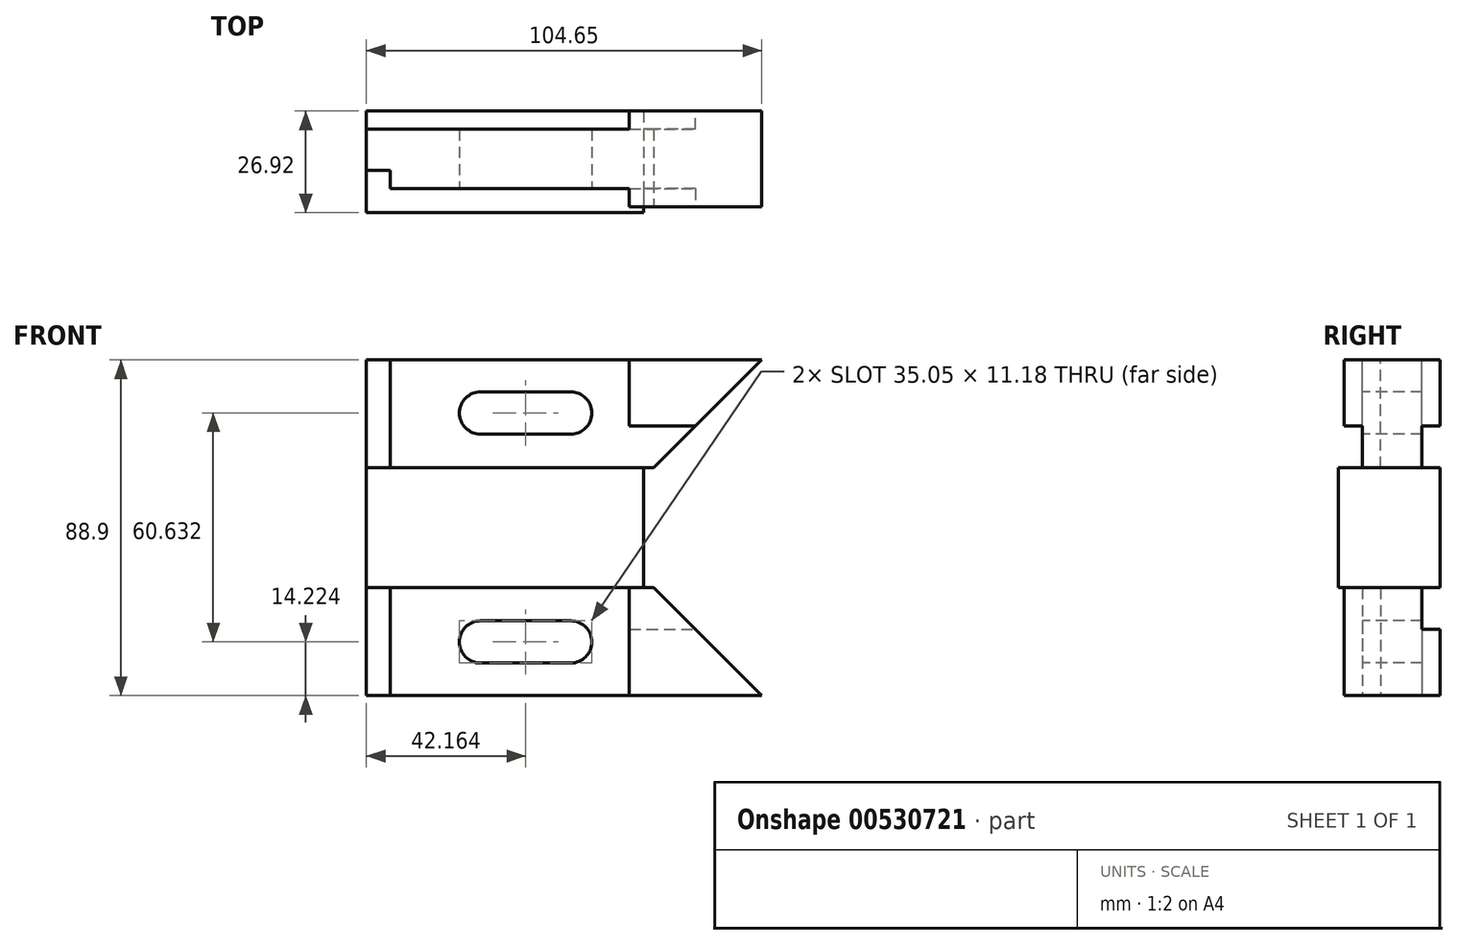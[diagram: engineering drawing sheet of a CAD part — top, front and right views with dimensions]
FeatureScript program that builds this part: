
annotation { "Feature Type Name" : "Feature", "Feature Type Description" : "" }
export const myFeature = defineFeature(function(context is Context, id is Id, definition is map)
    precondition{}
    {
        {
            var Q0;
            Q0=qCreatedBy(makeId("Right.planeOp"),FACE);
            var sketch = newSketch(context, id + "F0", { "sketchPlane" : qUnion([Q0])});
            skLineSegment(sketch, "E0", {"start": v(0, 0) * mm, "end": v(25.4, 0) * mm});
            skLineSegment(sketch, "E1", {"start": v(25.4, 0) * mm, "end": v(25.4, 28.58) * mm});
            skLineSegment(sketch, "E2", {"start": v(0, 0) * mm, "end": v(0, 28.58) * mm});
            skLineSegment(sketch, "E3", {"start": v(25.4, 60.33) * mm, "end": v(25.4, 88.9) * mm});
            skLineSegment(sketch, "E4", {"start": v(0, 60.33) * mm, "end": v(0, 88.9) * mm});
            skLineSegment(sketch, "E5", {"start": v(0, 88.9) * mm, "end": v(25.4, 88.9) * mm});
            skLineSegment(sketch, "E6", {"start": v(0, 28.58) * mm, "end": v(-1.52, 28.58) * mm});
            skLineSegment(sketch, "E7", {"start": v(-1.52, 28.58) * mm, "end": v(-1.52, 60.33) * mm});
            skLineSegment(sketch, "E8", {"start": v(0, 60.33) * mm, "end": v(-1.52, 60.33) * mm});
            skLineSegment(sketch, "E9", {"start": v(25.4, 60.33) * mm, "end": v(26.92, 60.33) * mm});
            skLineSegment(sketch, "E10", {"start": v(25.4, 28.58) * mm, "end": v(26.92, 28.58) * mm});
            skLineSegment(sketch, "E11", {"start": v(26.92, 60.33) * mm, "end": v(26.92, 28.58) * mm});
            skSolve(sketch);
        }
        {
            var Q0;
            Q0=qSketchRegion(id+"F0",true);
            extrude(context, id + "F1", {"entities" : qUnion([Q0]), "depth" : 104.65 * mm});
        }
        {
            var Q0;
            Q0=makeQuery(id+"F1.opExtrude","SWEPT_FACE",FACE,{"disambiguationData":[OSD([sQuery(id+"F0.wireOp",EDGE,"E5")])]});
            var sketch = newSketch(context, id + "F2", { "sketchPlane" : qUnion([Q0])});
            skLineSegment(sketch, "E12.0.0", {"start": v(0, 0) * mm, "end": v(0, -1.52) * mm});
            skLineSegment(sketch, "E12.0.1", {"start": v(0, -1.52) * mm, "end": v(104.65, -1.52) * mm});
            skLineSegment(sketch, "E12.0.2", {"start": v(104.65, -1.52) * mm, "end": v(104.65, 0) * mm});
            skLineSegment(sketch, "E12.0.3", {"start": v(104.65, 0) * mm, "end": v(0, 0) * mm});
            skLineSegment(sketch, "E13", {"start": v(0, -1.52) * mm, "end": v(0, 4.83) * mm});
            skLineSegment(sketch, "E14.0.0", {"start": v(0, 26.92) * mm, "end": v(0, 25.4) * mm});
            skLineSegment(sketch, "E14.0.1", {"start": v(0, 25.4) * mm, "end": v(104.65, 25.4) * mm});
            skLineSegment(sketch, "E14.0.2", {"start": v(104.65, 25.4) * mm, "end": v(104.65, 26.92) * mm});
            skLineSegment(sketch, "E14.0.3", {"start": v(104.65, 26.92) * mm, "end": v(0, 26.92) * mm});
            skLineSegment(sketch, "E15", {"start": v(0, 26.92) * mm, "end": v(0, 20.57) * mm});
            skLineSegment(sketch, "E16", {"start": v(0, 4.83) * mm, "end": v(0, 9.65) * mm});
            skLineSegment(sketch, "E17", {"start": v(0, 9.65) * mm, "end": v(6.35, 9.65) * mm});
            skLineSegment(sketch, "E18", {"start": v(6.35, 9.65) * mm, "end": v(6.35, 4.83) * mm});
            skLineSegment(sketch, "E19", {"start": v(6.35, 4.83) * mm, "end": v(69.6, 4.83) * mm});
            skLineSegment(sketch, "E20", {"start": v(0, 20.57) * mm, "end": v(69.6, 20.57) * mm});
            skLineSegment(sketch, "E21", {"start": v(69.6, 20.57) * mm, "end": v(69.6, 25.4) * mm});
            skLineSegment(sketch, "E22", {"start": v(69.6, 4.83) * mm, "end": v(69.6, 0) * mm});
            skLineSegment(sketch, "E23", {"start": v(0, -1.52) * mm, "end": v(73.4, -1.52) * mm});
            skLineSegment(sketch, "E24", {"start": v(73.4, -1.52) * mm, "end": v(73.4, 0) * mm});
            skLineSegment(sketch, "E25", {"start": v(73.4, 0) * mm, "end": v(0, 0) * mm});
            skLineSegment(sketch, "E26", {"start": v(0, 25.4) * mm, "end": v(0, 26.92) * mm});
            skLineSegment(sketch, "E27", {"start": v(0, 26.92) * mm, "end": v(73.4, 26.92) * mm});
            skLineSegment(sketch, "E28", {"start": v(73.4, 26.92) * mm, "end": v(73.4, 25.4) * mm});
            skLineSegment(sketch, "E29", {"start": v(73.4, 25.4) * mm, "end": v(0, 25.4) * mm});
            skSolve(sketch);
        }
        {
            var Q0;
            {var subQ0=sQuery(id+"F2.wireOp",EDGE,"E15");Q0=makeQuery(id+"F2.imprint","IMPRINT",FACE,{"disambiguationData":[TD([[makeQuery(id+"F2.imprint","IMPRINT",EDGE,{"derivedFrom":subQ0}),-1.0]])]});}
            var Q1;
            {var subQ0=sQuery(id+"F2.wireOp",EDGE,"E16");Q1=makeQuery(id+"F2.imprint","IMPRINT",FACE,{"disambiguationData":[TD([[makeQuery(id+"F2.imprint","IMPRINT",EDGE,{"derivedFrom":subQ0}),-1.0]])]});}
            extrude(context, id + "F3", {"entities" : qUnion([Q0, Q1]), "operationType" : NewBodyOperationType.REMOVE, "oppositeDirection" : true, "depth" : 28.57 * mm});
        }
        {
            var Q0;
            Q0=makeQuery(id+"F2.imprint","IMPRINT",FACE,{"disambiguationData":[TD([[makeQuery(id+"F2.imprint","IMPRINT",EDGE,{"derivedFrom":sQuery(id+"F2.wireOp",EDGE,"E14.0.1")}),-1.0]])]});
            var Q1;
            Q1=makeQuery(id+"F2.imprint","IMPRINT",FACE,{"disambiguationData":[TD([[makeQuery(id+"F2.imprint","IMPRINT",EDGE,{"derivedFrom":sQuery(id+"F2.wireOp",EDGE,"E12.0.1")}),1.0]])]});
            extrude(context, id + "F4", {"entities" : qUnion([Q0, Q1]), "operationType" : NewBodyOperationType.REMOVE, "oppositeDirection" : true, "depth" : 88.9 * mm});
        }
        {
            var Q0;
            Q0=makeQuery(id+"F1.opExtrude","SWEPT_FACE",FACE,{"disambiguationData":[OSD([sQuery(id+"F0.wireOp",EDGE,"E0")])]});
            var sketch = newSketch(context, id + "F5", { "sketchPlane" : qUnion([Q0])});
            skLineSegment(sketch, "E30.0", {"start": v(6.35, -4.83) * mm, "end": v(69.6, -4.83) * mm});
            skPoint(sketch, "E31.0", {"position": v(6.35, -9.65) * mm});
            skPoint(sketch, "E32.0", {"position": v(3.18, -9.65) * mm});
            skLineSegment(sketch, "E33.0", {"start": v(0, -9.65) * mm, "end": v(0, -20.57) * mm});
            skLineSegment(sketch, "E34.0", {"start": v(0, -20.57) * mm, "end": v(69.6, -20.57) * mm});
            skLineSegment(sketch, "E35.0", {"start": v(104.65, -25.4) * mm, "end": v(69.6, -25.4) * mm});
            skPoint(sketch, "E36.0", {"position": v(69.6, -22.99) * mm});
            skLineSegment(sketch, "E37.0", {"start": v(104.65, 0) * mm, "end": v(69.6, 0) * mm});
            skLineSegment(sketch, "E38.0", {"start": v(69.6, -4.83) * mm, "end": v(69.6, 0) * mm});
            skLineSegment(sketch, "E39.0", {"start": v(69.6, -20.57) * mm, "end": v(69.6, -25.4) * mm});
            skLineSegment(sketch, "E40.0.0", {"start": v(73.4, -25.4) * mm, "end": v(73.4, -26.92) * mm});
            skLineSegment(sketch, "E40.0.1", {"start": v(73.4, -26.92) * mm, "end": v(0, -26.92) * mm});
            skLineSegment(sketch, "E40.0.2", {"start": v(0, -26.92) * mm, "end": v(0, -20.57) * mm});
            skLineSegment(sketch, "E40.0.5", {"start": v(69.6, -25.4) * mm, "end": v(73.4, -25.4) * mm});
            skLineSegment(sketch, "E41.0.0", {"start": v(73.4, 1.52) * mm, "end": v(73.4, 0) * mm});
            skLineSegment(sketch, "E41.0.1", {"start": v(73.4, 0) * mm, "end": v(69.6, 0) * mm});
            skLineSegment(sketch, "E41.0.2", {"start": v(69.6, 0) * mm, "end": v(69.6, -4.83) * mm});
            skLineSegment(sketch, "E41.0.3", {"start": v(69.6, -4.83) * mm, "end": v(6.35, -4.83) * mm});
            skLineSegment(sketch, "E41.0.4", {"start": v(6.35, -4.83) * mm, "end": v(6.35, -9.65) * mm});
            skLineSegment(sketch, "E41.0.5", {"start": v(6.35, -9.65) * mm, "end": v(0, -9.65) * mm});
            skLineSegment(sketch, "E41.0.6", {"start": v(0, -9.65) * mm, "end": v(0, 1.52) * mm});
            skLineSegment(sketch, "E41.0.7", {"start": v(0, 1.52) * mm, "end": v(73.4, 1.52) * mm});
            skSolve(sketch);
        }
        {
            var Q0;
            Q0=qSketchRegion(id+"F5",true);
            extrude(context, id + "F6", {"entities" : qUnion([Q0]), "operationType" : NewBodyOperationType.REMOVE, "oppositeDirection" : true, "depth" : 28.57 * mm});
        }
        {
            var Q0;
            Q0=makeQuery(id+"F4.boolean.opBoolean","MERGE",FACE,{"derivedFrom":[makeQuery(id+"F1.opExtrude","SWEPT_FACE",FACE,{"disambiguationData":[OSD([sQuery(id+"F0.wireOp",EDGE,"E2")])]}),makeQuery(id+"F1.opExtrude","SWEPT_FACE",FACE,{"disambiguationData":[OSD([sQuery(id+"F0.wireOp",EDGE,"E4")])]}),makeQuery(id+"F4.opExtrude","SWEPT_FACE",FACE,{"disambiguationData":[OSD([sQuery(id+"F2.wireOp",EDGE,"E12.0.3")])]})]});
            var sketch = newSketch(context, id + "F7", { "sketchPlane" : qUnion([Q0])});
            skLineSegment(sketch, "E42.0", {"start": v(104.65, 88.9) * mm, "end": v(69.6, 88.9) * mm});
            skLineSegment(sketch, "E43.0", {"start": v(69.6, 71.37) * mm, "end": v(69.6, 88.9) * mm});
            skLineSegment(sketch, "E44.0", {"start": v(6.35, 88.9) * mm, "end": v(69.6, 88.9) * mm});
            skLineSegment(sketch, "E45.0.0", {"start": v(69.6, 88.9) * mm, "end": v(6.35, 88.9) * mm});
            skLineSegment(sketch, "E45.0.1", {"start": v(6.35, 88.9) * mm, "end": v(6.35, 60.33) * mm});
            skLineSegment(sketch, "E45.0.2", {"start": v(6.35, 60.33) * mm, "end": v(69.6, 60.33) * mm});
            skLineSegment(sketch, "E46.0.0", {"start": v(0, 28.58) * mm, "end": v(73.4, 28.58) * mm});
            skLineSegment(sketch, "E46.0.1", {"start": v(73.4, 28.58) * mm, "end": v(73.4, 60.33) * mm});
            skLineSegment(sketch, "E46.0.2", {"start": v(73.4, 60.33) * mm, "end": v(0, 60.33) * mm});
            skLineSegment(sketch, "E46.0.3", {"start": v(0, 60.33) * mm, "end": v(0, 28.58) * mm});
            skLineSegment(sketch, "E47.0.0", {"start": v(6.35, 0) * mm, "end": v(69.6, 0) * mm});
            skLineSegment(sketch, "E47.0.1", {"start": v(69.6, 0) * mm, "end": v(69.6, 28.58) * mm});
            skLineSegment(sketch, "E47.0.2", {"start": v(69.6, 28.58) * mm, "end": v(6.35, 28.58) * mm});
            skLineSegment(sketch, "E47.0.3", {"start": v(6.35, 28.58) * mm, "end": v(6.35, 0) * mm});
            skLineSegment(sketch, "E48.0.0", {"start": v(73.4, 60.33) * mm, "end": v(73.4, 28.58) * mm});
            skLineSegment(sketch, "E48.0.1", {"start": v(73.4, 28.58) * mm, "end": v(69.6, 28.58) * mm});
            skLineSegment(sketch, "E48.0.2", {"start": v(69.6, 28.58) * mm, "end": v(69.6, 0) * mm});
            skLineSegment(sketch, "E48.0.3", {"start": v(69.6, 0) * mm, "end": v(104.65, 0) * mm});
            skLineSegment(sketch, "E48.0.4", {"start": v(104.65, 0) * mm, "end": v(104.65, 88.9) * mm});
            skLineSegment(sketch, "E48.0.6", {"start": v(69.6, 88.9) * mm, "end": v(69.6, 60.33) * mm});
            skLineSegment(sketch, "E48.0.7", {"start": v(69.6, 60.33) * mm, "end": v(73.4, 60.33) * mm});
            skPoint(sketch, "E49.0", {"position": v(0, 14.29) * mm});
            skPoint(sketch, "E50.0", {"position": v(0, 74.61) * mm});
            skLineSegment(sketch, "E51.0", {"start": v(0, 60.33) * mm, "end": v(0, 88.9) * mm});
            skLineSegment(sketch, "E52.0", {"start": v(0, 88.9) * mm, "end": v(6.35, 88.9) * mm});
            skLineSegment(sketch, "E53", {"start": v(0, 88.9) * mm, "end": v(69.6, 88.9) * mm});
            skLineSegment(sketch, "E54", {"start": v(69.6, 88.9) * mm, "end": v(69.6, 71.37) * mm});
            skLineSegment(sketch, "E55", {"start": v(69.6, 71.37) * mm, "end": v(87.12, 71.37) * mm});
            skLineSegment(sketch, "E56", {"start": v(104.65, 88.9) * mm, "end": v(76.07, 60.33) * mm});
            skLineSegment(sketch, "E57", {"start": v(73.4, 60.33) * mm, "end": v(76.07, 60.33) * mm});
            skLineSegment(sketch, "E58", {"start": v(69.6, 0) * mm, "end": v(69.6, 14.29) * mm});
            skLineSegment(sketch, "E59", {"start": v(104.65, 44.45) * mm, "end": v(0, 44.45) * mm});
            skLineSegment(sketch, "E60.MirrorCS", {"start": v(104.65, 0) * mm, "end": v(76.07, 28.58) * mm});
            skLineSegment(sketch, "E61.MirrorCS", {"start": v(73.4, 28.58) * mm, "end": v(76.07, 28.58) * mm});
            skLineSegment(sketch, "E62.MirrorCS", {"start": v(69.6, 17.53) * mm, "end": v(87.12, 17.53) * mm});
            skSolve(sketch);
        }
        {
            var Q0;
            {var subQ5=sQuery(id+"F7.wireOp",EDGE,"E57");Q0=makeQuery(id+"F7.imprint","IMPRINT",FACE,{"disambiguationData":[TD([[makeQuery(id+"F7.imprint","IMPRINT",EDGE,{"derivedFrom":subQ5}),-1.0]])]});}
            var Q1;
            {var subQ8=sQuery(id+"F7.wireOp",EDGE,"E61.MirrorCS");Q1=makeQuery(id+"F7.imprint","IMPRINT",FACE,{"disambiguationData":[TD([[makeQuery(id+"F7.imprint","IMPRINT",EDGE,{"derivedFrom":subQ8}),1.0]])]});}
            extrude(context, id + "F8", {"entities" : qUnion([Q0, Q1]), "operationType" : NewBodyOperationType.REMOVE, "endBound" : BoundingType.THROUGH_ALL, "oppositeDirection" : true, "depth" : 25.4 * mm});
        }
        {
            var Q0;
            Q0=makeQuery(id+"F7.imprint","IMPRINT",FACE,{"disambiguationData":[TD([[makeQuery(id+"F7.imprint","IMPRINT",EDGE,{"derivedFrom":sQuery(id+"F7.wireOp",EDGE,"E48.0.6")}),-1.0]])]});
            var Q1;
            {var subQ1=sQuery(id+"F7.wireOp",EDGE,"E48.0.1");Q1=makeQuery(id+"F7.imprint","IMPRINT",FACE,{"disambiguationData":[TD([[makeQuery(id+"F7.imprint","IMPRINT",EDGE,{"derivedFrom":subQ1}),1.0]])]});}
            extrude(context, id + "F9", {"entities" : qUnion([Q0, Q1]), "operationType" : NewBodyOperationType.REMOVE, "oppositeDirection" : true, "depth" : 4.83 * mm});
        }
        {
            var Q0;
            Q0=makeQuery(id+"F8.boolean.opBoolean","SPLIT",FACE,{"disambiguationData":[TD([makeQuery(id+"F1.opExtrude","SWEPT_FACE",FACE,{"disambiguationData":[OSD([sQuery(id+"F0.wireOp",EDGE,"E0")])]})])],"derivedFrom":makeQuery(id+"F4.boolean.opBoolean","MERGE",FACE,{"derivedFrom":[makeQuery(id+"F1.opExtrude","SWEPT_FACE",FACE,{"disambiguationData":[OSD([sQuery(id+"F0.wireOp",EDGE,"E1")])]}),makeQuery(id+"F1.opExtrude","SWEPT_FACE",FACE,{"disambiguationData":[OSD([sQuery(id+"F0.wireOp",EDGE,"E3")])]}),makeQuery(id+"F4.opExtrude","SWEPT_FACE",FACE,{"disambiguationData":[OSD([sQuery(id+"F2.wireOp",EDGE,"E14.0.1")])]})]})});
            var sketch = newSketch(context, id + "F10", { "sketchPlane" : qUnion([Q0])});
            skLineSegment(sketch, "E63.0", {"start": v(-69.6, 71.37) * mm, "end": v(-87.12, 71.37) * mm});
            skLineSegment(sketch, "E64.0", {"start": v(-104.65, 88.9) * mm, "end": v(-76.07, 60.33) * mm});
            skLineSegment(sketch, "E65.0.0", {"start": v(-69.6, 60.33) * mm, "end": v(-73.4, 60.33) * mm});
            skLineSegment(sketch, "E65.0.1", {"start": v(-73.4, 60.33) * mm, "end": v(-76.07, 60.33) * mm});
            skLineSegment(sketch, "E65.0.2", {"start": v(-76.07, 60.33) * mm, "end": v(-87.12, 71.37) * mm});
            skLineSegment(sketch, "E65.0.3", {"start": v(-87.12, 71.37) * mm, "end": v(-69.6, 71.37) * mm});
            skLineSegment(sketch, "E65.0.4", {"start": v(-69.6, 71.37) * mm, "end": v(-69.6, 60.33) * mm});
            skLineSegment(sketch, "E66.0.0", {"start": v(-69.6, 28.58) * mm, "end": v(-69.6, 17.53) * mm});
            skLineSegment(sketch, "E66.0.1", {"start": v(-69.6, 17.53) * mm, "end": v(-87.12, 17.53) * mm});
            skLineSegment(sketch, "E66.0.2", {"start": v(-87.12, 17.53) * mm, "end": v(-76.07, 28.58) * mm});
            skLineSegment(sketch, "E66.0.3", {"start": v(-76.07, 28.58) * mm, "end": v(-73.4, 28.58) * mm});
            skLineSegment(sketch, "E66.0.4", {"start": v(-73.4, 28.58) * mm, "end": v(-69.6, 28.58) * mm});
            skSolve(sketch);
        }
        {
            var Q0;
            Q0=qSketchRegion(id+"F10",true);
            extrude(context, id + "F11", {"entities" : qUnion([Q0]), "operationType" : NewBodyOperationType.REMOVE, "oppositeDirection" : true, "depth" : 4.83 * mm});
        }
        {
            var Q0;
            Q0=makeQuery(id+"F7.imprint","IMPRINT",FACE,{"disambiguationData":[TD([[makeQuery(id+"F7.imprint","IMPRINT",EDGE,{"derivedFrom":sQuery(id+"F7.wireOp",EDGE,"E47.0.0")}),1.0]])]});
            var sketch = newSketch(context, id + "F12", { "sketchPlane" : qUnion([Q0])});
            skLineSegment(sketch, "E67", {"start": v(0, 0) * mm, "end": v(0, 14.22) * mm});
            skLineSegment(sketch, "E68", {"start": v(0, 0) * mm, "end": v(24.64, 0) * mm});
            skLineSegment(sketch, "E69", {"start": v(24.64, 0) * mm, "end": v(24.64, 14.22) * mm});
            skLineSegment(sketch, "E70", {"start": v(24.64, 14.22) * mm, "end": v(59.69, 14.22) * mm});
            skLineSegment(sketch, "E71", {"start": v(24.64, 14.22) * mm, "end": v(30.23, 14.22) * mm});
            skCircle(sketch, "E72", {"center": v(30.23, 14.22) * mm, "radius": 5.59 * mm});
            skCircle(sketch, "E73", {"center": v(54.1, 14.22) * mm, "radius": 5.59 * mm});
            skLineSegment(sketch, "E74", {"start": v(30.23, 19.81) * mm, "end": v(54.1, 19.81) * mm});
            skLineSegment(sketch, "E75", {"start": v(30.23, 8.64) * mm, "end": v(54.1, 8.64) * mm});
            skLineSegment(sketch, "E76", {"start": v(0, 44.54) * mm, "end": v(88.44, 44.54) * mm});
            skCircle(sketch, "E77.MirrorC", {"center": v(54.1, 74.86) * mm, "radius": 5.59 * mm});
            skLineSegment(sketch, "E78.MirrorCS", {"start": v(24.64, 74.86) * mm, "end": v(59.69, 74.86) * mm});
            skCircle(sketch, "E79.MirrorC", {"center": v(30.23, 74.86) * mm, "radius": 5.59 * mm});
            skLineSegment(sketch, "E80.MirrorCS", {"start": v(30.23, 80.44) * mm, "end": v(54.1, 80.44) * mm});
            skLineSegment(sketch, "E81.MirrorCS", {"start": v(30.23, 69.27) * mm, "end": v(54.1, 69.27) * mm});
            skSolve(sketch);
        }
        {
            var Q0;
            Q0=qSketchRegion(id+"F12",true);
            extrude(context, id + "F13", {"entities" : qUnion([Q0]), "operationType" : NewBodyOperationType.REMOVE, "endBound" : BoundingType.THROUGH_ALL, "oppositeDirection" : true, "depth" : 25.4 * mm});
        }
    });
